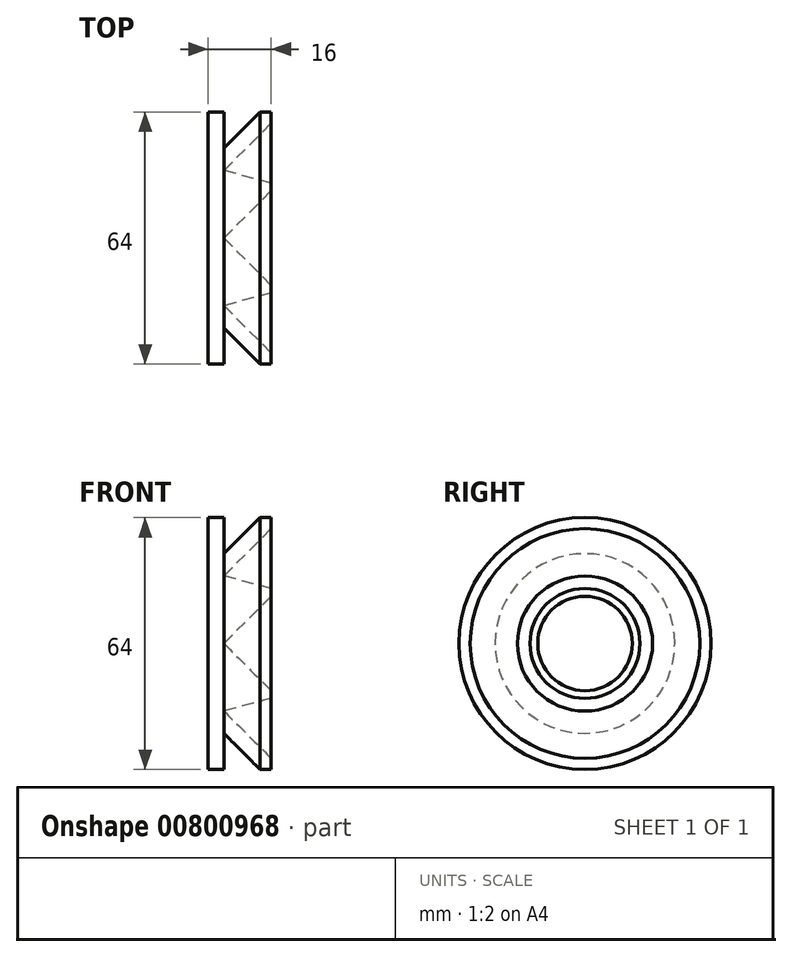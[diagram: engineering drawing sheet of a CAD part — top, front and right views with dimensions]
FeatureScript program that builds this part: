
annotation { "Feature Type Name" : "Feature", "Feature Type Description" : "" }
export const myFeature = defineFeature(function(context is Context, id is Id, definition is map)
    precondition{}
    {
        {
            var Q0;
            Q0=qCreatedBy(makeId("Top.planeOp"),FACE);
            var sketch = newSketch(context, id + "F0", { "sketchPlane" : qUnion([Q0])});
            skLineSegment(sketch, "E0", {"start": v(0, 0) * mm, "end": v(0, -32) * mm});
            skLineSegment(sketch, "E1", {"start": v(0, -32) * mm, "end": v(4, -32) * mm});
            skLineSegment(sketch, "E2", {"start": v(4, -32) * mm, "end": v(4, -22.83) * mm});
            skLineSegment(sketch, "E3", {"start": v(4, -22.83) * mm, "end": v(13.17, -32) * mm});
            skLineSegment(sketch, "E4", {"start": v(13.17, -32) * mm, "end": v(16, -32) * mm});
            skLineSegment(sketch, "E5", {"start": v(16, -32) * mm, "end": v(16, -29.17) * mm});
            skLineSegment(sketch, "E6", {"start": v(16, -29.17) * mm, "end": v(4, -17.17) * mm});
            skLineSegment(sketch, "E7", {"start": v(4, 0) * mm, "end": v(0, 0) * mm});
            skLineSegment(sketch, "E8", {"start": v(4, -5.66) * mm, "end": v(4, -13.03) * mm});
            skLineSegment(sketch, "E9", {"start": v(4, -13.03) * mm, "end": v(9.82, -11.47) * mm});
            skLineSegment(sketch, "E10", {"start": v(9.82, -11.47) * mm, "end": v(4, -5.66) * mm});
            skLineSegment(sketch, "E11", {"start": v(4, 0) * mm, "end": v(16, -12) * mm});
            skLineSegment(sketch, "E12", {"start": v(16, -12) * mm, "end": v(16, -13.96) * mm});
            skLineSegment(sketch, "E13", {"start": v(16, -13.96) * mm, "end": v(4, -17.17) * mm});
            skLineSegment(sketch, "E14", {"start": v(16, -29.17) * mm, "end": v(16, -13.96) * mm, "construction": true});
            skSolve(sketch);
        }
        {
            var Q0;
            Q0=makeQuery(id+"F0.imprint","IMPRINT",FACE,{"disambiguationData":[TD([[makeQuery(id+"F0.imprint","IMPRINT",EDGE,{"derivedFrom":sQuery(id+"F0.wireOp",EDGE,"E0")}),1.0]])]});
            var Q1;
            Q1=makeQuery(id+"F0.imprint","IMPRINT",FACE,{"disambiguationData":[TD([[makeQuery(id+"F0.imprint","IMPRINT",EDGE,{"derivedFrom":sQuery(id+"F0.wireOp",EDGE,"E8")}),1.0]])]});
            var Q2;
            Q2=sQuery(id+"F0.wireOp",EDGE,"E7");
            revolve(context, id + "F1", {"surfaceOperationType" : NewSurfaceOperationType.NEW, "entities" : qUnion([Q0, Q1]), "axis" : qUnion([Q2]), "revolveType" : RevolveType.FULL});
        }
    });
